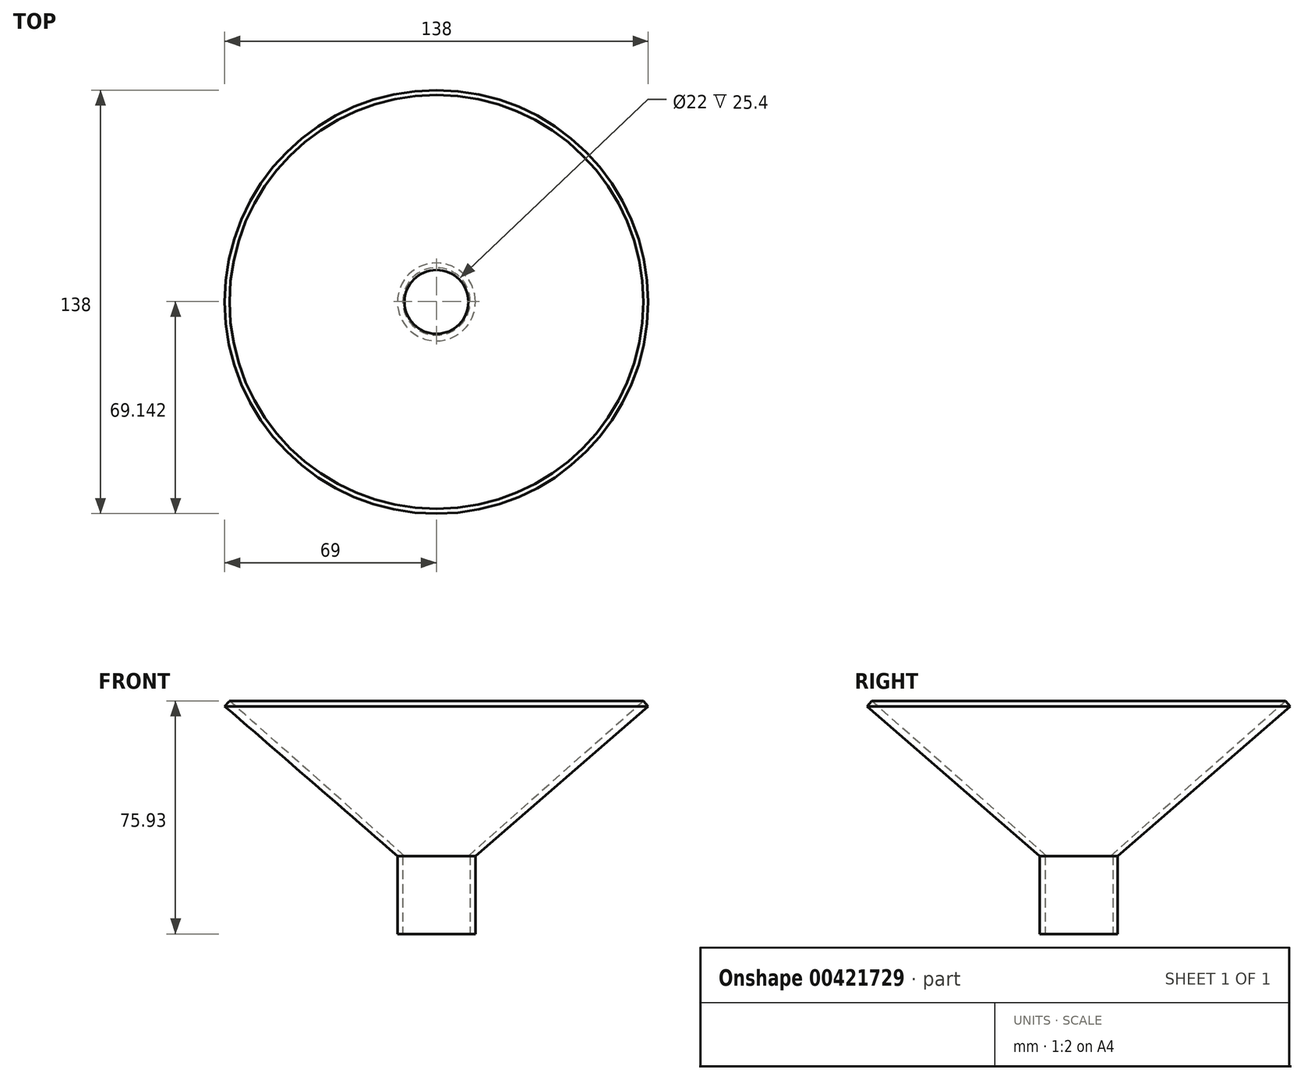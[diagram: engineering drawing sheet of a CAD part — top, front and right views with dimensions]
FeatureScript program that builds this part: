
annotation { "Feature Type Name" : "Feature", "Feature Type Description" : "" }
export const myFeature = defineFeature(function(context is Context, id is Id, definition is map)
    precondition{}
    {
        {
            var Q0;
            Q0=qCreatedBy(makeId("Right.planeOp"),FACE);
            var sketch = newSketch(context, id + "F0", { "sketchPlane" : qUnion([Q0])});
            skLineSegment(sketch, "E0", {"start": v(0, 0) * mm, "end": v(0, -25.4) * mm});
            skLineSegment(sketch, "E1", {"start": v(0, -25.4) * mm, "end": v(12.7, -25.4) * mm});
            skLineSegment(sketch, "E2", {"start": v(12.7, -25.4) * mm, "end": v(12.7, 0) * mm});
            skLineSegment(sketch, "E3", {"start": v(12.7, 0) * mm, "end": v(2.3, 0) * mm});
            skLineSegment(sketch, "E4", {"start": v(2.3, 0) * mm, "end": v(-54.74, 50.53) * mm});
            skLineSegment(sketch, "E5", {"start": v(-54.74, 50.53) * mm, "end": v(-56.3, 48.77) * mm});
            skLineSegment(sketch, "E6", {"start": v(-56.3, 48.77) * mm, "end": v(0, 0) * mm});
            skSolve(sketch);
        }
        {
            var Q0;
            Q0 = qSketchRegion(id + "F0", true);
            var Q1;
            Q1=sQuery(id+"F0.wireOp",EDGE,"E2");
            revolve(context, id + "F1", {"entities" : qUnion([Q0]), "axis" : qUnion([Q1]), "revolveType" : RevolveType.FULL});
        }
        {
            var Q0;
            Q0=makeQuery(id+"F1.opRevolve","SWEPT_FACE",FACE,{"disambiguationData":[OSD([sQuery(id+"F0.wireOp",EDGE,"E1")])]});
            var sketch = newSketch(context, id + "F2", { "sketchPlane" : qUnion([Q0])});
            skSolve(sketch);
        }
        {
            var Q0;
            Q0=makeQuery(id+"F2.imprint","IMPRINT",FACE,{"disambiguationData":[TD([[makeQuery(id+"F2.imprint","IMPRINT",EDGE,{"derivedFrom":makeQuery(id+"F1.opRevolve","SWEPT_EDGE",EDGE,{"disambiguationData":[OSD([sQuery(id+"F0.wireOp",EDGE,"E0"),sQuery(id+"F0.wireOp",EDGE,"E1")])]})}),1.0]])]});
            var sketch = newSketch(context, id + "F3", { "sketchPlane" : qUnion([Q0])});
            skCircle(sketch, "E7", {"center": v(0, -12.84) * mm, "radius": 11 * mm});
            skSolve(sketch);
        }
        {
            var Q0;
            Q0=makeQuery(id+"F3.imprint","IMPRINT",FACE,{"disambiguationData":[TD([[makeQuery(id+"F3.imprint","IMPRINT",EDGE,{"derivedFrom":sQuery(id+"F3.wireOp",EDGE,"E7")}),1.0]])]});
            extrude(context, id + "F4", {"entities" : qUnion([Q0]), "operationType" : NewBodyOperationType.REMOVE, "oppositeDirection" : true, "depth" : 25.4 * mm});
        }
    });
